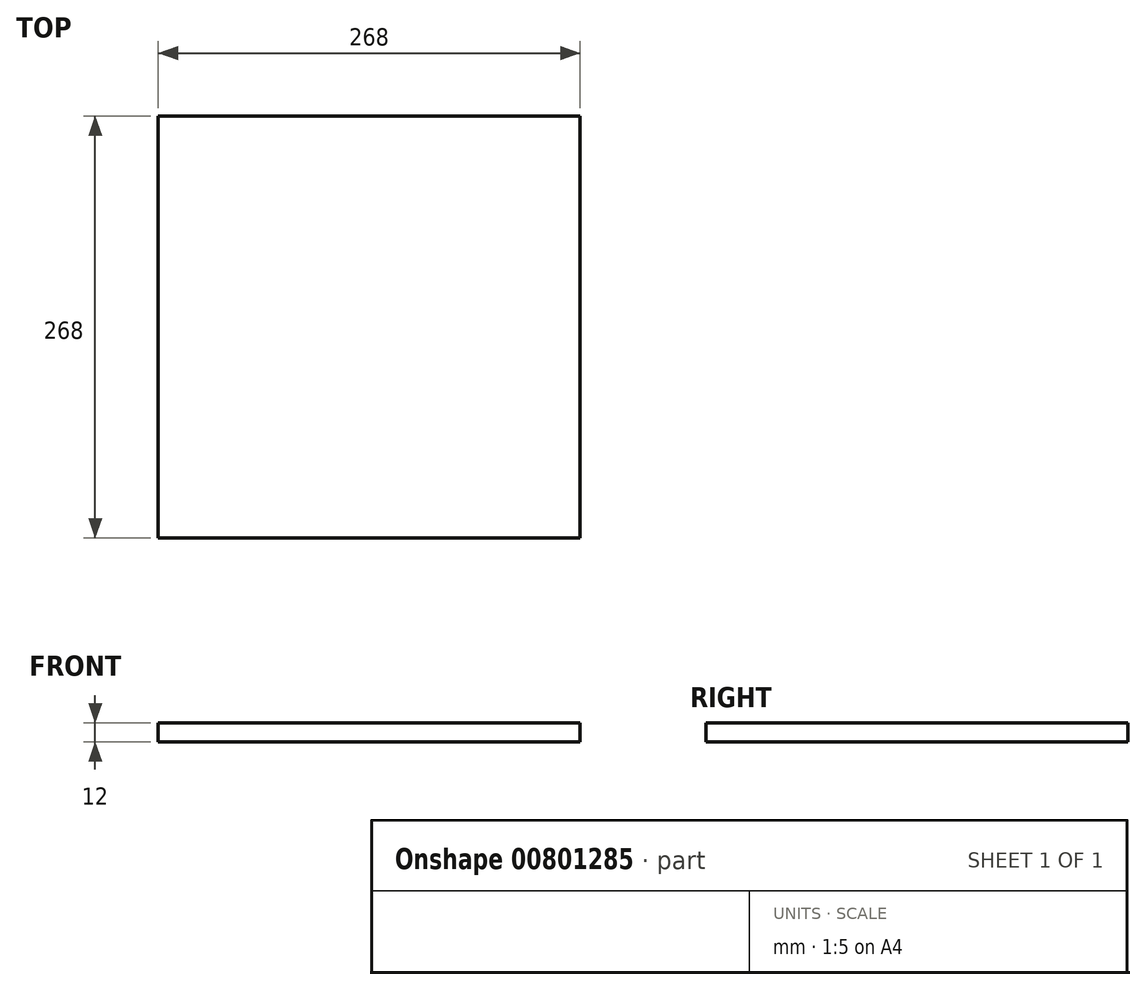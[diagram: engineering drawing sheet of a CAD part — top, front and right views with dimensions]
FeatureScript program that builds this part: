
annotation { "Feature Type Name" : "Feature", "Feature Type Description" : "" }
export const myFeature = defineFeature(function(context is Context, id is Id, definition is map)
    precondition{}
    {
        {
            var Q0;
            Q0=qCreatedBy(makeId("Top.planeOp"),FACE);
            var sketch = newSketch(context, id + "F0", { "sketchPlane" : qUnion([Q0])});
            skLineSegment(sketch, "E0.bottom", {"start": v(-134, -134) * mm, "end": v(134, -134) * mm});
            skLineSegment(sketch, "E0.top", {"start": v(-134, 134) * mm, "end": v(134, 134) * mm});
            skLineSegment(sketch, "E0.left", {"start": v(-134, -134) * mm, "end": v(-134, 134) * mm});
            skLineSegment(sketch, "E0.right", {"start": v(134, -134) * mm, "end": v(134, 134) * mm});
            skPoint(sketch, "E0.middle", {"position": v(0, 0) * mm});
            skSolve(sketch);
        }
        {
            var Q0;
            Q0=makeQuery(id+"F0.imprint","IMPRINT",FACE,{"disambiguationData":[TD([[makeQuery(id+"F0.imprint","IMPRINT",EDGE,{"derivedFrom":sQuery(id+"F0.wireOp",EDGE,"E0.bottom")}),1.0]])]});
            extrude(context, id + "F1", {"entities" : qUnion([Q0]), "depth" : 12 * mm, "offsetDistance" : 25 * mm});
        }
    });
